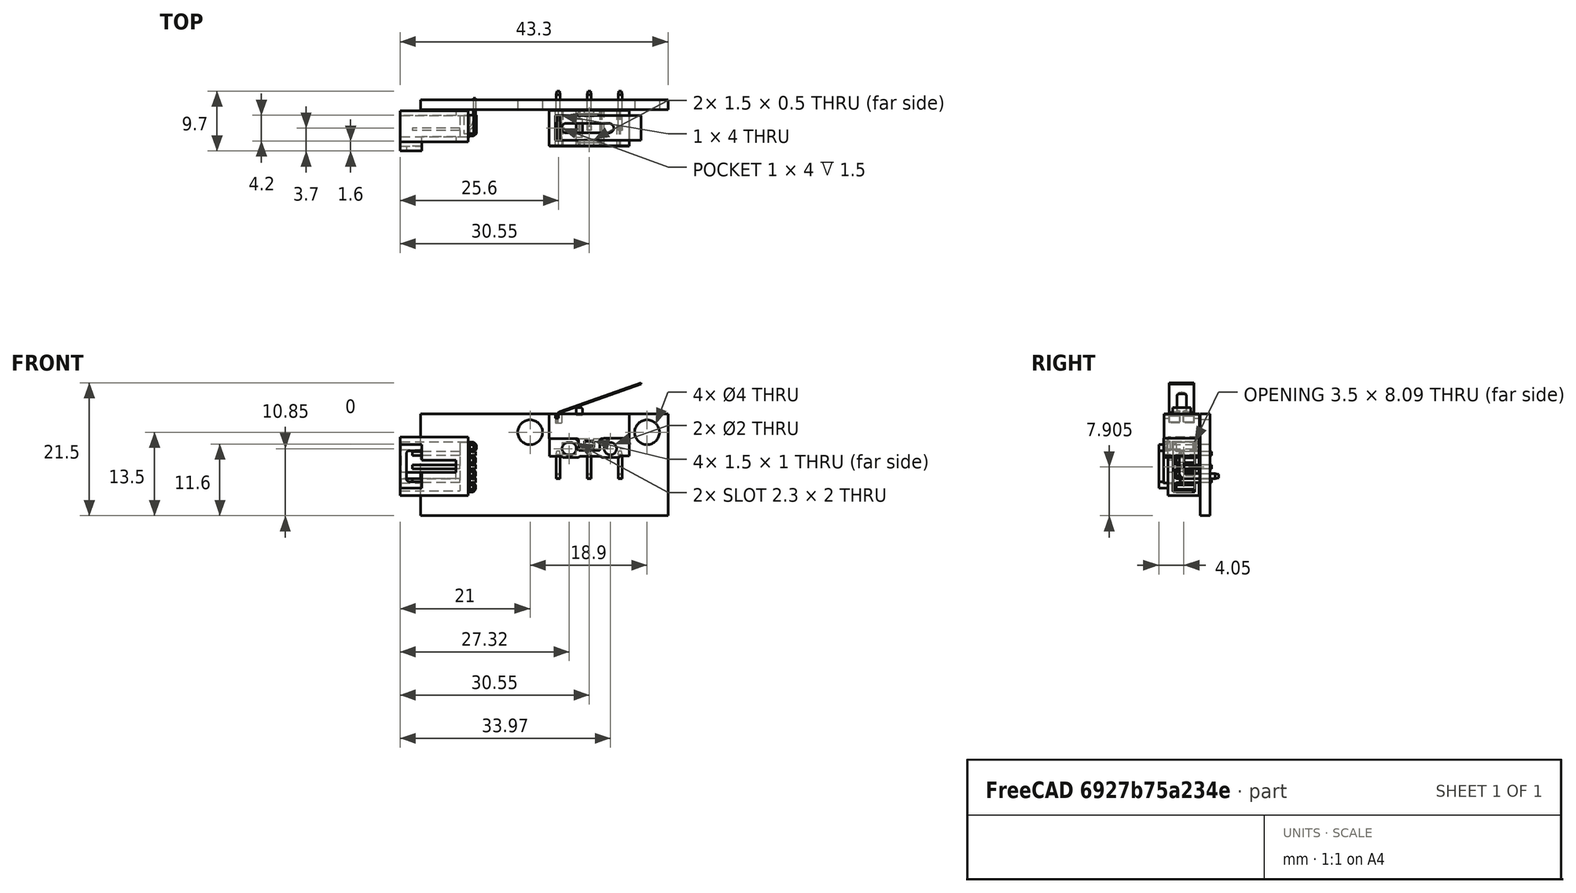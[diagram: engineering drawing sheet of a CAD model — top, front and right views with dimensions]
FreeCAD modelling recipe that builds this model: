
FCSTD DOCUMENT  (FreeCAD 0.14R3702 (Git))
Label: endstop
License: CC-BY 3.0
LicenseURL: http://creativecommons.org/licenses/by/3.0/
objects: Part::Cut×4, Part::MultiFuse×3, Part::Cylinder×2, Part::Fillet×2, Part::Box×1, Part::FeaturePython×1, App::DocumentObjectGroup×1, Part::Compound×1
note: 14 computed .brp shape members not serialized (recipe doc carries the construction recipe); baked Part::Feature solids carry a one-line shape summary decoded from their .brp

FEATURE [Part::Box] Box  label="prePlaca"
  Height = 16.5
  Length = 40
  Width = 1.6
FEATURE [Part::Cylinder] Cylinder  label="Cilindro"
  Angle = 360
  Height = 10
  Placement = pos=(17.7,8,13.5) rot=(1,0,0;1.5708rad)
  Radius = 2
FEATURE [Part::Cylinder] Cylinder001  label="Cilindro001"
  Angle = 360
  Height = 10
  Placement = pos=(36.6,8,13.5) rot=(1,0,0;1.5708rad)
  Radius = 2
FEATURE [Part::Cut] Cut001
  Base = -> Box
  Tool = -> Cylinder
FEATURE [Part::Cut] Cut002  label="Placa"
  Base = -> Cut001
  Tool = -> Cylinder001
FEATURE [Part::Fillet] Fillet  label="Cuerpo"
  Edges = 4 edges r=0.4: [Edge27,Edge29,Edge33,Edge35]
  Placement = pos=(27.25,-3,12.5) rot=(0,0,1;0rad)
FEATURE [Part::MultiFuse] Fusion  label="base"
  Placement = pos=(27.25,-3,12.5) rot=(0,0,1;0rad)
FEATURE [Part::Cut] Cut  label="Palanca"
  Placement = pos=(27.25,-3,12.5) rot=(0,0,1;0rad)
FEATURE [Part::FeaturePython] Array  label="Pines"  # Draft array (typed FeaturePython)
  Angle = 360
  ArrayType = 0
  Axis = (0,0,1)
  Center = (0,0,0)
  IntervalX = (5,0,0)
  IntervalY = (0,1,0)
  IntervalZ = (0,0,1)
  NumberPolar = 1
  NumberX = 3
  NumberY = 1
  NumberZ = 1
  Placement = pos=(22.25,-3,12.5) rot=(0,0,1;0rad)
FEATURE [Part::Fillet] Fillet001  label="pulsador"
  Edges = 2 edges r=0.3: [Edge2,Edge6]
  Placement = pos=(27.25,-3,12.5) rot=(0,0,1;0rad)
FEATURE [App::DocumentObjectGroup] Grupo  label="GR_EndStop"
  Group = -> [Fillet,Fusion,Cut,Array,Fillet001]
FEATURE [Part::MultiFuse] Fusion002  label="Conectores"
  Placement = pos=(0,0.7,0.7) rot=(0,0,1;1.5708rad)
FEATURE [Part::Cut] Cut003  label="AlojaConectores"
  Placement = pos=(0,0.7,0.7) rot=(0,0,1;1.5708rad)
FEATURE [Part::MultiFuse] Fusion001  label="Conector3pin"
  Placement = pos=(15,1.5,8) rot=(0.57735,0.57735,-0.57735;2.0944rad)
  Shapes = -> [Fusion002,Cut003]
FEATURE [Part::Compound] Compound  label="endstop-final"
